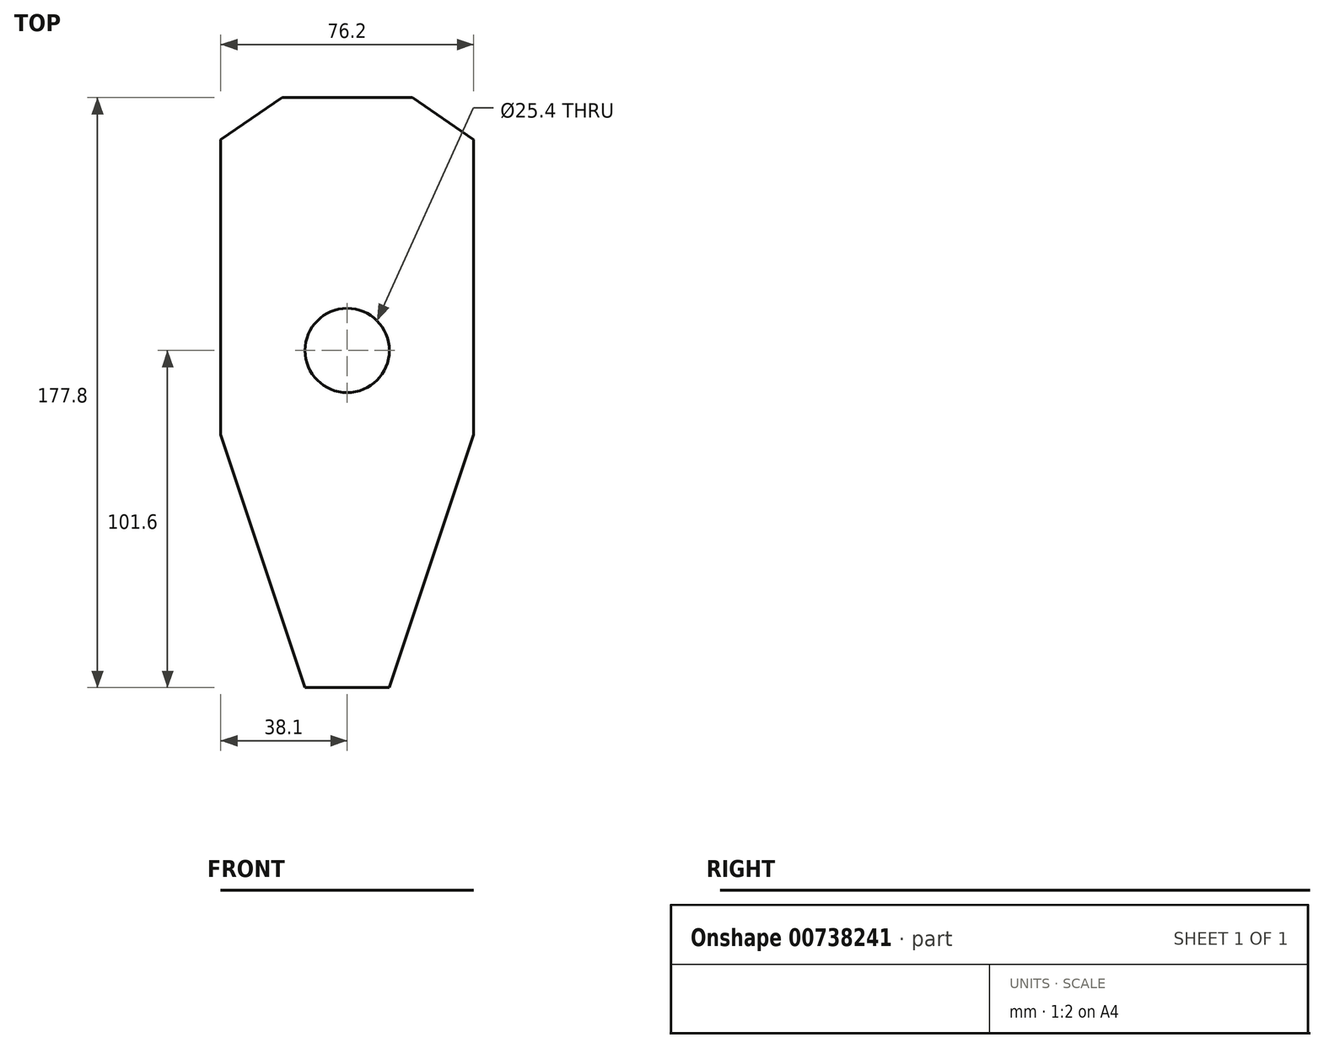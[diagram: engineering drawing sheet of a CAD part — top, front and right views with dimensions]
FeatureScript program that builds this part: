
annotation { "Feature Type Name" : "Feature", "Feature Type Description" : "" }
export const myFeature = defineFeature(function(context is Context, id is Id, definition is map)
    precondition{}
    {
        {
            var Q0;
            Q0=qCreatedBy(makeId("Top.planeOp"),FACE);
            var sketch = newSketch(context, id + "F0", { "sketchPlane" : qUnion([Q0])});
            skLineSegment(sketch, "E0", {"start": v(-12.7, -76.2) * mm, "end": v(12.7, -76.2) * mm});
            skLineSegment(sketch, "E1", {"start": v(0, 0) * mm, "end": v(0, -76.2) * mm, "construction": true});
            skLineSegment(sketch, "E2", {"start": v(12.7, -76.2) * mm, "end": v(38.1, -76.2) * mm, "construction": true});
            skLineSegment(sketch, "E3", {"start": v(38.1, -76.2) * mm, "end": v(38.1, 0) * mm, "construction": true});
            skLineSegment(sketch, "E4", {"start": v(-12.7, -76.2) * mm, "end": v(-38.1, -76.2) * mm, "construction": true});
            skLineSegment(sketch, "E5", {"start": v(-38.1, -76.2) * mm, "end": v(-38.1, 0) * mm, "construction": true});
            skLineSegment(sketch, "E6", {"start": v(-38.1, 0) * mm, "end": v(-12.7, -76.2) * mm});
            skLineSegment(sketch, "E7", {"start": v(12.7, -76.2) * mm, "end": v(38.1, 0) * mm});
            skLineSegment(sketch, "E8", {"start": v(38.1, 0) * mm, "end": v(38.1, 50.8) * mm});
            skLineSegment(sketch, "E9", {"start": v(-38.1, 0) * mm, "end": v(-38.1, 50.8) * mm});
            skCircle(sketch, "E10", {"center": v(0, 25.4) * mm, "radius": 25.4 * mm, "construction": true});
            skPoint(sketch, "E11", {"position": v(38.1, 25.4) * mm});
            skPoint(sketch, "E12", {"position": v(-38.1, 25.4) * mm});
            skLineSegment(sketch, "E13", {"start": v(25.4, 25.4) * mm, "end": v(38.1, 25.4) * mm, "construction": true});
            skLineSegment(sketch, "E14", {"start": v(-25.4, 25.4) * mm, "end": v(-38.1, 25.4) * mm, "construction": true});
            skLineSegment(sketch, "E15", {"start": v(-38.1, 50.8) * mm, "end": v(-38.1, 88.9) * mm});
            skLineSegment(sketch, "E16", {"start": v(-38.1, 88.9) * mm, "end": v(38.1, 88.9) * mm, "construction": true});
            skLineSegment(sketch, "E17", {"start": v(38.1, 88.9) * mm, "end": v(38.1, 50.8) * mm});
            skPoint(sketch, "E18", {"position": v(0, 88.9) * mm});
            skLineSegment(sketch, "E19", {"start": v(-19.61, 101.6) * mm, "end": v(19.61, 101.6) * mm});
            skLineSegment(sketch, "E20", {"start": v(19.61, 101.6) * mm, "end": v(38.1, 88.9) * mm});
            skLineSegment(sketch, "E21", {"start": v(-19.61, 101.6) * mm, "end": v(-38.1, 88.9) * mm});
            skCircle(sketch, "E22", {"center": v(0, 25.4) * mm, "radius": 12.7 * mm});
            skSolve(sketch);
        }
        {
            var Q0;
            Q0=makeQuery(id+"F0.imprint","IMPRINT",FACE,{"disambiguationData":[TD([[makeQuery(id+"F0.imprint","IMPRINT",EDGE,{"derivedFrom":sQuery(id+"F0.wireOp",EDGE,"E0")}),1.0]])]});
            extrude(context, id + "F1", {"entities" : qUnion([Q0]), "oppositeDirection" : true, "depth" : 1 / 203.2 * mm, "offsetDistance" : 25.4 * mm});
        }
    });
